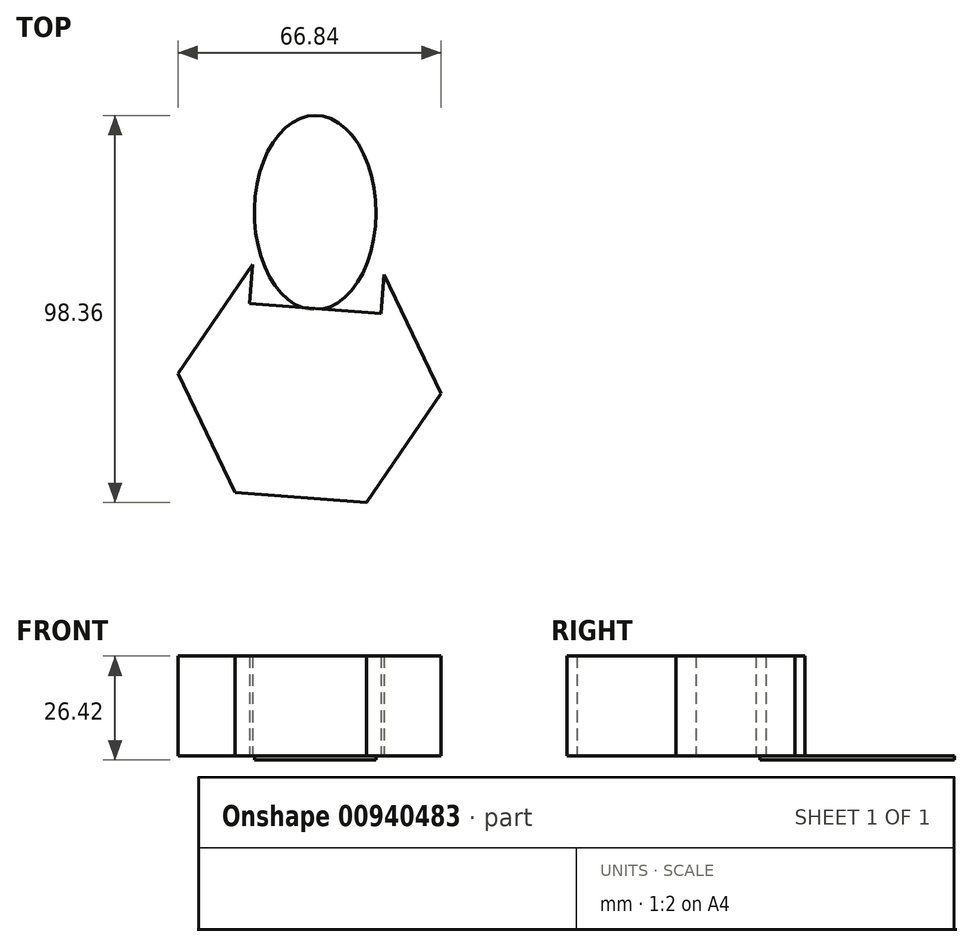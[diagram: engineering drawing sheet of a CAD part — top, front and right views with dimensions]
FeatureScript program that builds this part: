
annotation { "Feature Type Name" : "Feature", "Feature Type Description" : "" }
export const myFeature = defineFeature(function(context is Context, id is Id, definition is map)
    precondition{}
    {
        {
            var Q0;
            Q0=qCreatedBy(makeId("Top.planeOp"),FACE);
            var sketch = newSketch(context, id + "F0", { "sketchPlane" : qUnion([Q0])});
            skCircle(sketch, "E0.cCircle", {"center": v(-64.76, 39.7) * mm, "radius": 29.03 * mm, "construction": true});
            skLineSegment(sketch, "E0.0", {"start": v(-83.7, 12.05) * mm, "end": v(-98.18, 42.27) * mm});
            skLineSegment(sketch, "E0.1", {"start": v(-98.18, 42.27) * mm, "end": v(-79.25, 69.93) * mm});
            skLineSegment(sketch, "E0.2", {"start": v(-79.25, 69.93) * mm, "end": v(-45.83, 67.37) * mm});
            skLineSegment(sketch, "E0.3", {"start": v(-45.83, 67.37) * mm, "end": v(-31.34, 37.14) * mm});
            skLineSegment(sketch, "E0.4", {"start": v(-31.34, 37.14) * mm, "end": v(-50.28, 9.49) * mm});
            skLineSegment(sketch, "E0.5", {"start": v(-50.28, 9.49) * mm, "end": v(-83.7, 12.05) * mm});
            skPoint(sketch, "E0.0.midPoint", {"position": v(-90.94, 27.16) * mm});
            skSolve(sketch);
        }
        {
            var Q0;
            Q0=qCreatedBy(makeId("Top.planeOp"),FACE);
            var sketch = newSketch(context, id + "F1", { "sketchPlane" : qUnion([Q0])});
            skArc(sketch, "E1", {"start": v(-79.53, 69.79) * mm, "mid": v(-63.4, 59.38) * mm, "end": v(-45.91, 67.3) * mm});
            skSolve(sketch);
        }
        {
            var Q0;
            Q0=makeQuery(id+"F0.imprint","IMPRINT",FACE,{"disambiguationData":[TD([[makeQuery(id+"F0.imprint","IMPRINT",EDGE,{"derivedFrom":sQuery(id+"F0.wireOp",EDGE,"E0.0")}),-1.0]])]});
            extrude(context, id + "F2", {"entities" : qUnion([Q0]), "depth" : 25.4 * mm, "offsetDistance" : 25.4 * mm});
        }
        {
            var Q0;
            Q0=sQuery(id+"F1.wireOp",EDGE,"E1");
            extrude(context, id + "F3", {"bodyType" : ToolBodyType.SURFACE, "surfaceEntities" : qUnion([Q0]), "depth" : 25.4 * mm, "offsetDistance" : 25.4 * mm});
        }
        {
            var Q0;
            Q0=makeQuery(id+"F2.opExtrude","SWEPT_FACE",FACE,{"disambiguationData":[OSD([sQuery(id+"F0.wireOp",EDGE,"E0.2")])]});
            extrude(context, id + "F4", {"entities" : qUnion([Q0]), "operationType" : NewBodyOperationType.REMOVE, "oppositeDirection" : true, "depth" : 9.9 * mm, "offsetDistance" : 25.4 * mm});
        }
        {
            var Q0;
            Q0=qCreatedBy(makeId("Top.planeOp"),FACE);
            var sketch = newSketch(context, id + "F5", { "sketchPlane" : qUnion([Q0])});
            skEllipse(sketch, "E2", {"center": v(-63.34, 83.17) * mm, "majorRadius": 24.68 * mm, "minorRadius": 15.45 * mm, "majorAxis": v(0, 1)});
            skSolve(sketch);
        }
        {
            var Q0;
            Q0=makeQuery(id+"F5.imprint","IMPRINT",FACE,{"disambiguationData":[TD([[makeQuery(id+"F5.imprint","IMPRINT",EDGE,{"derivedFrom":sQuery(id+"F5.wireOp",EDGE,"E2")}),1.0]])]});
            extrude(context, id + "F6", {"entities" : qUnion([Q0]), "operationType" : NewBodyOperationType.ADD, "oppositeDirection" : true, "depth" : 1.02 * mm, "offsetDistance" : 25.4 * mm});
        }
    });
